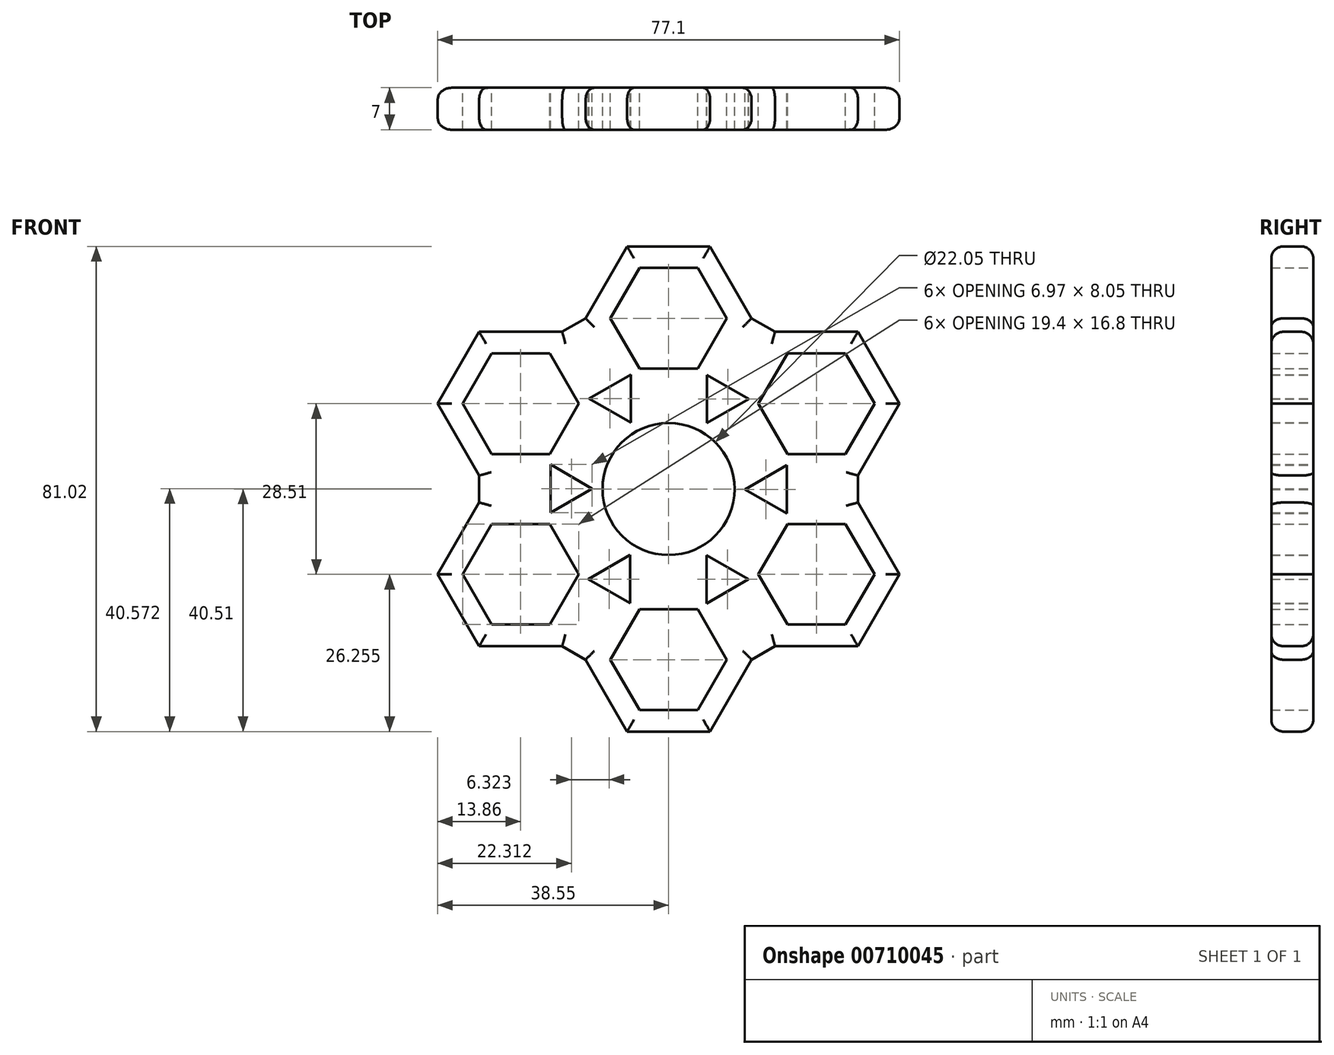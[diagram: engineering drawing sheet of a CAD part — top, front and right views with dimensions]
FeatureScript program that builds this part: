
annotation { "Feature Type Name" : "Feature", "Feature Type Description" : "" }
export const myFeature = defineFeature(function(context is Context, id is Id, definition is map)
    precondition{}
    {
        {
            var Q0;
            Q0=qCreatedBy(makeId("Front.planeOp"),FACE);
            var sketch = newSketch(context, id + "F0", { "sketchPlane" : qUnion([Q0])});
            skCircle(sketch, "E0", {"center": v(0, 0) * mm, "radius": 14.5 * mm});
            skCircle(sketch, "E1", {"center": v(0, 0) * mm, "radius": 11.03 * mm});
            skCircle(sketch, "E2.cCircle", {"center": v(0, 28.5) * mm, "radius": 8.4 * mm, "construction": true});
            skLineSegment(sketch, "E2.0", {"start": v(4.85, 20.1) * mm, "end": v(-4.85, 20.1) * mm});
            skLineSegment(sketch, "E2.1", {"start": v(-4.85, 20.1) * mm, "end": v(-9.7, 28.5) * mm});
            skLineSegment(sketch, "E2.2", {"start": v(-9.7, 28.5) * mm, "end": v(-4.85, 36.9) * mm});
            skLineSegment(sketch, "E2.3", {"start": v(-4.85, 36.9) * mm, "end": v(4.85, 36.9) * mm});
            skLineSegment(sketch, "E2.4", {"start": v(4.85, 36.9) * mm, "end": v(9.7, 28.5) * mm});
            skLineSegment(sketch, "E2.5", {"start": v(9.7, 28.5) * mm, "end": v(4.85, 20.1) * mm});
            skPoint(sketch, "E2.0.midPoint", {"position": v(0, 20.1) * mm});
            skCircle(sketch, "E3.cCircle", {"center": v(0, 28.5) * mm, "radius": 12 * mm, "construction": true});
            skLineSegment(sketch, "E3.0", {"start": v(6.93, 16.5) * mm, "end": v(-6.93, 16.5) * mm});
            skLineSegment(sketch, "E3.1", {"start": v(-6.93, 16.5) * mm, "end": v(-13.86, 28.5) * mm});
            skLineSegment(sketch, "E3.2", {"start": v(-13.86, 28.5) * mm, "end": v(-6.93, 40.5) * mm});
            skLineSegment(sketch, "E3.3", {"start": v(-6.93, 40.5) * mm, "end": v(6.93, 40.5) * mm});
            skLineSegment(sketch, "E3.4", {"start": v(6.93, 40.5) * mm, "end": v(13.86, 28.5) * mm});
            skLineSegment(sketch, "E3.5", {"start": v(13.86, 28.5) * mm, "end": v(6.93, 16.5) * mm});
            skPoint(sketch, "E3.0.midPoint", {"position": v(0, 16.5) * mm});
            skLineSegment(sketch, "E4.1.0", {"start": v(-17.76, 26.25) * mm, "end": v(-10.83, 14.25) * mm});
            skPoint(sketch, "E4.1.2", {"position": v(-17.42, 10.05) * mm});
            skLineSegment(sketch, "E4.1.3", {"start": v(-31.62, 2.25) * mm, "end": v(-38.55, 14.25) * mm});
            skLineSegment(sketch, "E4.1.4", {"start": v(-17.76, 2.25) * mm, "end": v(-31.62, 2.25) * mm});
            skCircle(sketch, "E4.1.5", {"center": v(-24.7, 14.25) * mm, "radius": 12 * mm, "construction": true});
            skPoint(sketch, "E4.1.7", {"position": v(-14.3, 8.25) * mm});
            skCircle(sketch, "E4.1.8", {"center": v(-24.7, 14.25) * mm, "radius": 8.4 * mm, "construction": true});
            skLineSegment(sketch, "E4.1.9", {"start": v(-29.54, 22.65) * mm, "end": v(-19.84, 22.65) * mm});
            skLineSegment(sketch, "E4.1.10", {"start": v(-29.54, 5.85) * mm, "end": v(-34.39, 14.25) * mm});
            skLineSegment(sketch, "E4.1.11", {"start": v(-38.55, 14.25) * mm, "end": v(-31.62, 26.25) * mm});
            skLineSegment(sketch, "E4.1.12", {"start": v(-10.83, 14.25) * mm, "end": v(-17.76, 2.25) * mm});
            skLineSegment(sketch, "E4.1.13", {"start": v(-15, 14.25) * mm, "end": v(-19.84, 5.85) * mm});
            skLineSegment(sketch, "E4.1.14", {"start": v(-19.84, 22.65) * mm, "end": v(-15, 14.25) * mm});
            skLineSegment(sketch, "E4.1.15", {"start": v(-31.62, 26.25) * mm, "end": v(-17.76, 26.25) * mm});
            skLineSegment(sketch, "E4.1.16", {"start": v(-34.39, 14.25) * mm, "end": v(-29.54, 22.65) * mm});
            skLineSegment(sketch, "E4.1.17", {"start": v(-19.84, 5.85) * mm, "end": v(-29.54, 5.85) * mm});
            skLineSegment(sketch, "E4.2.0", {"start": v(-31.62, -2.25) * mm, "end": v(-17.76, -2.25) * mm});
            skPoint(sketch, "E4.2.2", {"position": v(-17.42, -10.05) * mm});
            skLineSegment(sketch, "E4.2.3", {"start": v(-17.76, -26.25) * mm, "end": v(-31.62, -26.25) * mm});
            skLineSegment(sketch, "E4.2.4", {"start": v(-10.83, -14.25) * mm, "end": v(-17.76, -26.25) * mm});
            skCircle(sketch, "E4.2.5", {"center": v(-24.7, -14.25) * mm, "radius": 12 * mm, "construction": true});
            skPoint(sketch, "E4.2.7", {"position": v(-14.3, -8.25) * mm});
            skCircle(sketch, "E4.2.8", {"center": v(-24.7, -14.25) * mm, "radius": 8.4 * mm, "construction": true});
            skLineSegment(sketch, "E4.2.9", {"start": v(-34.39, -14.25) * mm, "end": v(-29.54, -5.85) * mm});
            skLineSegment(sketch, "E4.2.10", {"start": v(-19.84, -22.65) * mm, "end": v(-29.54, -22.65) * mm});
            skLineSegment(sketch, "E4.2.11", {"start": v(-31.62, -26.25) * mm, "end": v(-38.55, -14.25) * mm});
            skLineSegment(sketch, "E4.2.12", {"start": v(-17.76, -2.25) * mm, "end": v(-10.83, -14.25) * mm});
            skLineSegment(sketch, "E4.2.13", {"start": v(-19.84, -5.85) * mm, "end": v(-15, -14.25) * mm});
            skLineSegment(sketch, "E4.2.14", {"start": v(-29.54, -5.85) * mm, "end": v(-19.84, -5.85) * mm});
            skLineSegment(sketch, "E4.2.15", {"start": v(-38.55, -14.25) * mm, "end": v(-31.62, -2.25) * mm});
            skLineSegment(sketch, "E4.2.16", {"start": v(-29.54, -22.65) * mm, "end": v(-34.39, -14.25) * mm});
            skLineSegment(sketch, "E4.2.17", {"start": v(-15, -14.25) * mm, "end": v(-19.84, -22.65) * mm});
            skLineSegment(sketch, "E4.3.0", {"start": v(-13.86, -28.5) * mm, "end": v(-6.93, -16.5) * mm});
            skPoint(sketch, "E4.3.2", {"position": v(0, -20.1) * mm});
            skLineSegment(sketch, "E4.3.3", {"start": v(13.86, -28.5) * mm, "end": v(6.93, -40.5) * mm});
            skLineSegment(sketch, "E4.3.4", {"start": v(6.93, -16.5) * mm, "end": v(13.86, -28.5) * mm});
            skCircle(sketch, "E4.3.5", {"center": v(0, -28.5) * mm, "radius": 12 * mm, "construction": true});
            skPoint(sketch, "E4.3.7", {"position": v(0, -16.5) * mm});
            skCircle(sketch, "E4.3.8", {"center": v(0, -28.5) * mm, "radius": 8.4 * mm, "construction": true});
            skLineSegment(sketch, "E4.3.9", {"start": v(-4.85, -36.9) * mm, "end": v(-9.7, -28.5) * mm});
            skLineSegment(sketch, "E4.3.10", {"start": v(9.7, -28.5) * mm, "end": v(4.85, -36.9) * mm});
            skLineSegment(sketch, "E4.3.11", {"start": v(6.93, -40.5) * mm, "end": v(-6.93, -40.5) * mm});
            skLineSegment(sketch, "E4.3.12", {"start": v(-6.93, -16.5) * mm, "end": v(6.93, -16.5) * mm});
            skLineSegment(sketch, "E4.3.13", {"start": v(-4.85, -20.1) * mm, "end": v(4.85, -20.1) * mm});
            skLineSegment(sketch, "E4.3.14", {"start": v(-9.7, -28.5) * mm, "end": v(-4.85, -20.1) * mm});
            skLineSegment(sketch, "E4.3.15", {"start": v(-6.93, -40.5) * mm, "end": v(-13.86, -28.5) * mm});
            skLineSegment(sketch, "E4.3.16", {"start": v(4.85, -36.9) * mm, "end": v(-4.85, -36.9) * mm});
            skLineSegment(sketch, "E4.3.17", {"start": v(4.85, -20.1) * mm, "end": v(9.7, -28.5) * mm});
            skLineSegment(sketch, "E4.4.0", {"start": v(17.76, -26.25) * mm, "end": v(10.83, -14.25) * mm});
            skPoint(sketch, "E4.4.2", {"position": v(17.42, -10.05) * mm});
            skLineSegment(sketch, "E4.4.3", {"start": v(31.62, -2.25) * mm, "end": v(38.55, -14.25) * mm});
            skLineSegment(sketch, "E4.4.4", {"start": v(17.76, -2.25) * mm, "end": v(31.62, -2.25) * mm});
            skCircle(sketch, "E4.4.5", {"center": v(24.7, -14.25) * mm, "radius": 12 * mm, "construction": true});
            skPoint(sketch, "E4.4.7", {"position": v(14.3, -8.25) * mm});
            skCircle(sketch, "E4.4.8", {"center": v(24.7, -14.25) * mm, "radius": 8.4 * mm, "construction": true});
            skLineSegment(sketch, "E4.4.9", {"start": v(29.54, -22.65) * mm, "end": v(19.84, -22.65) * mm});
            skLineSegment(sketch, "E4.4.10", {"start": v(29.54, -5.85) * mm, "end": v(34.39, -14.25) * mm});
            skLineSegment(sketch, "E4.4.11", {"start": v(38.55, -14.25) * mm, "end": v(31.62, -26.25) * mm});
            skLineSegment(sketch, "E4.4.12", {"start": v(10.83, -14.25) * mm, "end": v(17.76, -2.25) * mm});
            skLineSegment(sketch, "E4.4.13", {"start": v(15, -14.25) * mm, "end": v(19.84, -5.85) * mm});
            skLineSegment(sketch, "E4.4.14", {"start": v(19.84, -22.65) * mm, "end": v(15, -14.25) * mm});
            skLineSegment(sketch, "E4.4.15", {"start": v(31.62, -26.25) * mm, "end": v(17.76, -26.25) * mm});
            skLineSegment(sketch, "E4.4.16", {"start": v(34.39, -14.25) * mm, "end": v(29.54, -22.65) * mm});
            skLineSegment(sketch, "E4.4.17", {"start": v(19.84, -5.85) * mm, "end": v(29.54, -5.85) * mm});
            skLineSegment(sketch, "E4.5.0", {"start": v(31.62, 2.25) * mm, "end": v(17.76, 2.25) * mm});
            skPoint(sketch, "E4.5.2", {"position": v(17.42, 10.05) * mm});
            skLineSegment(sketch, "E4.5.3", {"start": v(17.76, 26.25) * mm, "end": v(31.62, 26.25) * mm});
            skLineSegment(sketch, "E4.5.4", {"start": v(10.83, 14.25) * mm, "end": v(17.76, 26.25) * mm});
            skCircle(sketch, "E4.5.5", {"center": v(24.7, 14.25) * mm, "radius": 12 * mm, "construction": true});
            skPoint(sketch, "E4.5.7", {"position": v(14.3, 8.25) * mm});
            skCircle(sketch, "E4.5.8", {"center": v(24.7, 14.25) * mm, "radius": 8.4 * mm, "construction": true});
            skLineSegment(sketch, "E4.5.9", {"start": v(34.39, 14.25) * mm, "end": v(29.54, 5.85) * mm});
            skLineSegment(sketch, "E4.5.10", {"start": v(19.84, 22.65) * mm, "end": v(29.54, 22.65) * mm});
            skLineSegment(sketch, "E4.5.11", {"start": v(31.62, 26.25) * mm, "end": v(38.55, 14.25) * mm});
            skLineSegment(sketch, "E4.5.12", {"start": v(17.76, 2.25) * mm, "end": v(10.83, 14.25) * mm});
            skLineSegment(sketch, "E4.5.13", {"start": v(19.84, 5.85) * mm, "end": v(15, 14.25) * mm});
            skLineSegment(sketch, "E4.5.14", {"start": v(29.54, 5.85) * mm, "end": v(19.84, 5.85) * mm});
            skLineSegment(sketch, "E4.5.15", {"start": v(38.55, 14.25) * mm, "end": v(31.62, 2.25) * mm});
            skLineSegment(sketch, "E4.5.16", {"start": v(29.54, 22.65) * mm, "end": v(34.39, 14.25) * mm});
            skLineSegment(sketch, "E4.5.17", {"start": v(15, 14.25) * mm, "end": v(19.84, 22.65) * mm});
            skLineSegment(sketch, "E5", {"start": v(13.86, 28.5) * mm, "end": v(17.76, 26.25) * mm});
            skLineSegment(sketch, "E6.1.0", {"start": v(-17.76, 26.25) * mm, "end": v(-13.86, 28.5) * mm});
            skLineSegment(sketch, "E6.2.0", {"start": v(-31.62, -2.25) * mm, "end": v(-31.62, 2.25) * mm});
            skLineSegment(sketch, "E6.3.0", {"start": v(-13.86, -28.5) * mm, "end": v(-17.76, -26.25) * mm});
            skLineSegment(sketch, "E6.4.0", {"start": v(17.76, -26.25) * mm, "end": v(13.86, -28.5) * mm});
            skLineSegment(sketch, "E6.5.0", {"start": v(31.62, 2.25) * mm, "end": v(31.62, -2.25) * mm});
            skSolve(sketch);
        }
        {
            var Q0;
            Q0 = qSketchRegion(id + "F0", true);
            var Q1;
            Q1=makeQuery(id+"F0.imprint","IMPRINT",FACE,{"disambiguationData":[TD([[makeQuery(id+"F0.imprint","IMPRINT",EDGE,{"derivedFrom":sQuery(id+"F0.wireOp",EDGE,"E0")}),1.0]])]});
            extrude(context, id + "F1", {"entities" : qUnion([Q0, Q1]), "depth" : 7 * mm, "offsetDistance" : 25 * mm});
        }
        {
            var Q0;
            Q0=makeQuery(id+"F1.opExtrude","CAP_EDGE",EDGE,{"disambiguationData":[OSD([sQuery(id+"F0.wireOp",EDGE,"E3.3")])],"isStart":false});
            var Q1;
            Q1=makeQuery(id+"F1.opExtrude","CAP_EDGE",EDGE,{"disambiguationData":[OSD([sQuery(id+"F0.wireOp",EDGE,"E3.4")])],"isStart":false});
            var Q2;
            Q2=makeQuery(id+"F1.opExtrude","CAP_EDGE",EDGE,{"disambiguationData":[OSD([sQuery(id+"F0.wireOp",EDGE,"6zvGGHwx-PwQj-7mVk-bG3N-4MqW4xq4l6px")])],"isStart":false});
            var Q3;
            Q3=makeQuery(id+"F1.opExtrude","CAP_EDGE",EDGE,{"disambiguationData":[OSD([sQuery(id+"F0.wireOp",EDGE,"E4.5.3")])],"isStart":false});
            var Q4;
            Q4=makeQuery(id+"F1.opExtrude","CAP_EDGE",EDGE,{"disambiguationData":[OSD([sQuery(id+"F0.wireOp",EDGE,"E4.5.11")])],"isStart":false});
            var Q5;
            Q5=makeQuery(id+"F1.opExtrude","CAP_EDGE",EDGE,{"disambiguationData":[OSD([sQuery(id+"F0.wireOp",EDGE,"E4.5.15")])],"isStart":false});
            var Q6;
            Q6=makeQuery(id+"F1.opExtrude","CAP_EDGE",EDGE,{"disambiguationData":[OSD([sQuery(id+"F0.wireOp",EDGE,"2094d824-f66e-4dc5-9a7e-ccef21a2b5a5.5.0")])],"isStart":false});
            var Q7;
            Q7=makeQuery(id+"F1.opExtrude","CAP_EDGE",EDGE,{"disambiguationData":[OSD([sQuery(id+"F0.wireOp",EDGE,"E4.4.3")])],"isStart":false});
            var Q8;
            Q8=makeQuery(id+"F1.opExtrude","CAP_EDGE",EDGE,{"disambiguationData":[OSD([sQuery(id+"F0.wireOp",EDGE,"E4.4.11")])],"isStart":false});
            var Q9;
            Q9=makeQuery(id+"F1.opExtrude","CAP_EDGE",EDGE,{"disambiguationData":[OSD([sQuery(id+"F0.wireOp",EDGE,"E4.4.15")])],"isStart":false});
            var Q10;
            Q10=makeQuery(id+"F1.opExtrude","CAP_EDGE",EDGE,{"disambiguationData":[OSD([sQuery(id+"F0.wireOp",EDGE,"2094d824-f66e-4dc5-9a7e-ccef21a2b5a5.4.0")])],"isStart":false});
            var Q11;
            Q11=makeQuery(id+"F1.opExtrude","CAP_EDGE",EDGE,{"disambiguationData":[OSD([sQuery(id+"F0.wireOp",EDGE,"E4.3.3")])],"isStart":false});
            var Q12;
            Q12=makeQuery(id+"F1.opExtrude","CAP_EDGE",EDGE,{"disambiguationData":[OSD([sQuery(id+"F0.wireOp",EDGE,"E4.3.11")])],"isStart":false});
            var Q13;
            Q13=makeQuery(id+"F1.opExtrude","CAP_EDGE",EDGE,{"disambiguationData":[OSD([sQuery(id+"F0.wireOp",EDGE,"E4.3.15")])],"isStart":false});
            var Q14;
            Q14=makeQuery(id+"F1.opExtrude","CAP_EDGE",EDGE,{"disambiguationData":[OSD([sQuery(id+"F0.wireOp",EDGE,"2094d824-f66e-4dc5-9a7e-ccef21a2b5a5.3.0")])],"isStart":false});
            var Q15;
            Q15=makeQuery(id+"F1.opExtrude","CAP_EDGE",EDGE,{"disambiguationData":[OSD([sQuery(id+"F0.wireOp",EDGE,"E4.2.3")])],"isStart":false});
            var Q16;
            Q16=makeQuery(id+"F1.opExtrude","CAP_EDGE",EDGE,{"disambiguationData":[OSD([sQuery(id+"F0.wireOp",EDGE,"E4.2.11")])],"isStart":false});
            var Q17;
            Q17=makeQuery(id+"F1.opExtrude","CAP_EDGE",EDGE,{"disambiguationData":[OSD([sQuery(id+"F0.wireOp",EDGE,"E4.2.15")])],"isStart":false});
            var Q18;
            Q18=makeQuery(id+"F1.opExtrude","CAP_EDGE",EDGE,{"disambiguationData":[OSD([sQuery(id+"F0.wireOp",EDGE,"2094d824-f66e-4dc5-9a7e-ccef21a2b5a5.2.0")])],"isStart":false});
            var Q19;
            Q19=makeQuery(id+"F1.opExtrude","CAP_EDGE",EDGE,{"disambiguationData":[OSD([sQuery(id+"F0.wireOp",EDGE,"E4.1.3")])],"isStart":false});
            var Q20;
            Q20=makeQuery(id+"F1.opExtrude","CAP_EDGE",EDGE,{"disambiguationData":[OSD([sQuery(id+"F0.wireOp",EDGE,"E4.1.11")])],"isStart":false});
            var Q21;
            Q21=makeQuery(id+"F1.opExtrude","CAP_EDGE",EDGE,{"disambiguationData":[OSD([sQuery(id+"F0.wireOp",EDGE,"E4.1.15")])],"isStart":false});
            var Q22;
            Q22=makeQuery(id+"F1.opExtrude","CAP_EDGE",EDGE,{"disambiguationData":[OSD([sQuery(id+"F0.wireOp",EDGE,"2094d824-f66e-4dc5-9a7e-ccef21a2b5a5.1.0")])],"isStart":false});
            var Q23;
            Q23=makeQuery(id+"F1.opExtrude","CAP_EDGE",EDGE,{"disambiguationData":[OSD([sQuery(id+"F0.wireOp",EDGE,"E3.2")])],"isStart":false});
            var Q24;
            Q24=makeQuery(id+"F1.opExtrude","CAP_EDGE",EDGE,{"disambiguationData":[OSD([sQuery(id+"F0.wireOp",EDGE,"2094d824-f66e-4dc5-9a7e-ccef21a2b5a5.3.0")])],"isStart":true});
            var Q25;
            Q25=makeQuery(id+"F1.opExtrude","CAP_EDGE",EDGE,{"disambiguationData":[OSD([sQuery(id+"F0.wireOp",EDGE,"E4.3.15")])],"isStart":true});
            var Q26;
            Q26=makeQuery(id+"F1.opExtrude","CAP_EDGE",EDGE,{"disambiguationData":[OSD([sQuery(id+"F0.wireOp",EDGE,"E4.3.3")])],"isStart":true});
            var Q27;
            Q27=makeQuery(id+"F1.opExtrude","CAP_EDGE",EDGE,{"disambiguationData":[OSD([sQuery(id+"F0.wireOp",EDGE,"2094d824-f66e-4dc5-9a7e-ccef21a2b5a5.4.0")])],"isStart":true});
            var Q28;
            Q28=makeQuery(id+"F1.opExtrude","CAP_EDGE",EDGE,{"disambiguationData":[OSD([sQuery(id+"F0.wireOp",EDGE,"E4.4.15")])],"isStart":true});
            var Q29;
            Q29=makeQuery(id+"F1.opExtrude","CAP_EDGE",EDGE,{"disambiguationData":[OSD([sQuery(id+"F0.wireOp",EDGE,"E4.4.11")])],"isStart":true});
            var Q30;
            Q30=makeQuery(id+"F1.opExtrude","CAP_EDGE",EDGE,{"disambiguationData":[OSD([sQuery(id+"F0.wireOp",EDGE,"E4.4.3")])],"isStart":true});
            var Q31;
            Q31=makeQuery(id+"F1.opExtrude","CAP_EDGE",EDGE,{"disambiguationData":[OSD([sQuery(id+"F0.wireOp",EDGE,"2094d824-f66e-4dc5-9a7e-ccef21a2b5a5.5.0")])],"isStart":true});
            var Q32;
            Q32=makeQuery(id+"F1.opExtrude","CAP_EDGE",EDGE,{"disambiguationData":[OSD([sQuery(id+"F0.wireOp",EDGE,"E4.5.15")])],"isStart":true});
            var Q33;
            Q33=makeQuery(id+"F1.opExtrude","CAP_EDGE",EDGE,{"disambiguationData":[OSD([sQuery(id+"F0.wireOp",EDGE,"E4.5.11")])],"isStart":true});
            var Q34;
            Q34=makeQuery(id+"F1.opExtrude","CAP_EDGE",EDGE,{"disambiguationData":[OSD([sQuery(id+"F0.wireOp",EDGE,"E4.5.3")])],"isStart":true});
            var Q35;
            Q35=makeQuery(id+"F1.opExtrude","CAP_EDGE",EDGE,{"disambiguationData":[OSD([sQuery(id+"F0.wireOp",EDGE,"6zvGGHwx-PwQj-7mVk-bG3N-4MqW4xq4l6px")])],"isStart":true});
            var Q36;
            Q36=makeQuery(id+"F1.opExtrude","CAP_EDGE",EDGE,{"disambiguationData":[OSD([sQuery(id+"F0.wireOp",EDGE,"E3.4")])],"isStart":true});
            var Q37;
            Q37=makeQuery(id+"F1.opExtrude","CAP_EDGE",EDGE,{"disambiguationData":[OSD([sQuery(id+"F0.wireOp",EDGE,"2094d824-f66e-4dc5-9a7e-ccef21a2b5a5.1.0")])],"isStart":true});
            var Q38;
            Q38=makeQuery(id+"F1.opExtrude","CAP_EDGE",EDGE,{"disambiguationData":[OSD([sQuery(id+"F0.wireOp",EDGE,"E4.1.15")])],"isStart":true});
            var Q39;
            Q39=makeQuery(id+"F1.opExtrude","CAP_EDGE",EDGE,{"disambiguationData":[OSD([sQuery(id+"F0.wireOp",EDGE,"E4.1.11")])],"isStart":true});
            var Q40;
            Q40=makeQuery(id+"F1.opExtrude","CAP_EDGE",EDGE,{"disambiguationData":[OSD([sQuery(id+"F0.wireOp",EDGE,"E4.1.3")])],"isStart":true});
            var Q41;
            Q41=makeQuery(id+"F1.opExtrude","CAP_EDGE",EDGE,{"disambiguationData":[OSD([sQuery(id+"F0.wireOp",EDGE,"2094d824-f66e-4dc5-9a7e-ccef21a2b5a5.2.0")])],"isStart":true});
            var Q42;
            Q42=makeQuery(id+"F1.opExtrude","CAP_EDGE",EDGE,{"disambiguationData":[OSD([sQuery(id+"F0.wireOp",EDGE,"E4.2.15")])],"isStart":true});
            var Q43;
            Q43=makeQuery(id+"F1.opExtrude","CAP_EDGE",EDGE,{"disambiguationData":[OSD([sQuery(id+"F0.wireOp",EDGE,"E4.2.11")])],"isStart":true});
            var Q44;
            Q44=makeQuery(id+"F1.opExtrude","CAP_EDGE",EDGE,{"disambiguationData":[OSD([sQuery(id+"F0.wireOp",EDGE,"E4.2.3")])],"isStart":true});
            var Q45;
            Q45=makeQuery(id+"F1.opExtrude","CAP_EDGE",EDGE,{"disambiguationData":[OSD([sQuery(id+"F0.wireOp",EDGE,"E4.3.11")])],"isStart":true});
            var Q46;
            Q46=makeQuery(id+"F1.opExtrude","CAP_EDGE",EDGE,{"disambiguationData":[OSD([sQuery(id+"F0.wireOp",EDGE,"E3.2")])],"isStart":true});
            var Q47;
            Q47=makeQuery(id+"F1.opExtrude","CAP_EDGE",EDGE,{"disambiguationData":[OSD([sQuery(id+"F0.wireOp",EDGE,"E3.3")])],"isStart":true});
            var Q48;
            Q48=makeQuery(id+"F1.opExtrude","CAP_EDGE",EDGE,{"disambiguationData":[OSD([sQuery(id+"F0.wireOp",EDGE,"E6.1.0")])],"isStart":false});
            var Q49;
            Q49=makeQuery(id+"F1.opExtrude","CAP_EDGE",EDGE,{"disambiguationData":[OSD([sQuery(id+"F0.wireOp",EDGE,"E5")])],"isStart":false});
            var Q50;
            Q50=makeQuery(id+"F1.opExtrude","CAP_EDGE",EDGE,{"disambiguationData":[OSD([sQuery(id+"F0.wireOp",EDGE,"E6.5.0")])],"isStart":false});
            var Q51;
            Q51=makeQuery(id+"F1.opExtrude","CAP_EDGE",EDGE,{"disambiguationData":[OSD([sQuery(id+"F0.wireOp",EDGE,"E6.4.0")])],"isStart":false});
            var Q52;
            Q52=makeQuery(id+"F1.opExtrude","CAP_EDGE",EDGE,{"disambiguationData":[OSD([sQuery(id+"F0.wireOp",EDGE,"E6.3.0")])],"isStart":false});
            var Q53;
            Q53=makeQuery(id+"F1.opExtrude","CAP_EDGE",EDGE,{"disambiguationData":[OSD([sQuery(id+"F0.wireOp",EDGE,"E6.2.0")])],"isStart":false});
            var Q54;
            Q54=makeQuery(id+"F1.opExtrude","CAP_EDGE",EDGE,{"disambiguationData":[OSD([sQuery(id+"F0.wireOp",EDGE,"E6.1.0")])],"isStart":true});
            var Q55;
            Q55=makeQuery(id+"F1.opExtrude","CAP_EDGE",EDGE,{"disambiguationData":[OSD([sQuery(id+"F0.wireOp",EDGE,"E5")])],"isStart":true});
            var Q56;
            Q56=makeQuery(id+"F1.opExtrude","CAP_EDGE",EDGE,{"disambiguationData":[OSD([sQuery(id+"F0.wireOp",EDGE,"E6.5.0")])],"isStart":true});
            var Q57;
            Q57=makeQuery(id+"F1.opExtrude","CAP_EDGE",EDGE,{"disambiguationData":[OSD([sQuery(id+"F0.wireOp",EDGE,"E6.4.0")])],"isStart":true});
            var Q58;
            Q58=makeQuery(id+"F1.opExtrude","CAP_EDGE",EDGE,{"disambiguationData":[OSD([sQuery(id+"F0.wireOp",EDGE,"E6.3.0")])],"isStart":true});
            var Q59;
            Q59=makeQuery(id+"F1.opExtrude","CAP_EDGE",EDGE,{"disambiguationData":[OSD([sQuery(id+"F0.wireOp",EDGE,"E6.2.0")])],"isStart":true});
            fillet(context, id + "F2", {"entities" : qUnion([Q0, Q1, Q2, Q3, Q4, Q5, Q6, Q7, Q8, Q9, Q10, Q11, Q12, Q13, Q14, Q15, Q16, Q17, Q18, Q19, Q20, Q21, Q22, Q23, Q24, Q25, Q26, Q27, Q28, Q29, Q30, Q31, Q32, Q33, Q34, Q35, Q36, Q37, Q38, Q39, Q40, Q41, Q42, Q43, Q44, Q45, Q46, Q47, Q48, Q49, Q50, Q51, Q52, Q53, Q54, Q55, Q56, Q57, Q58, Q59]), "radius" : 2 * mm, "tangentPropagation" : true, "allowEdgeOverflow" : false});
        }
        {
            var Q0;
            Q0=qCreatedBy(makeId("Front.planeOp"),FACE);
            var sketch = newSketch(context, id + "F3", { "sketchPlane" : qUnion([Q0])});
            skCircle(sketch, "E7.cCircle", {"center": v(-8.65, 15.1) * mm, "radius": 2.32 * mm, "construction": true});
            skLineSegment(sketch, "E7.0", {"start": v(-6.32, 19.12) * mm, "end": v(-6.32, 11.08) * mm});
            skLineSegment(sketch, "E7.1", {"start": v(-6.32, 11.08) * mm, "end": v(-13.3, 15.1) * mm});
            skLineSegment(sketch, "E7.2", {"start": v(-13.3, 15.1) * mm, "end": v(-6.32, 19.12) * mm});
            skPoint(sketch, "E7.0.midPoint", {"position": v(-6.32, 15.1) * mm});
            skCircle(sketch, "E8.1.0", {"center": v(-17.4, 0.06) * mm, "radius": 2.32 * mm, "construction": true});
            skLineSegment(sketch, "E8.1.1", {"start": v(-19.72, -3.96) * mm, "end": v(-19.72, 4.08) * mm});
            skLineSegment(sketch, "E8.1.2", {"start": v(-12.75, 0.06) * mm, "end": v(-19.72, -3.96) * mm});
            skLineSegment(sketch, "E8.1.3", {"start": v(-19.72, 4.08) * mm, "end": v(-12.75, 0.06) * mm});
            skCircle(sketch, "E8.2.0", {"center": v(-8.75, -15.04) * mm, "radius": 2.32 * mm, "construction": true});
            skLineSegment(sketch, "E8.2.1", {"start": v(-6.43, -19.06) * mm, "end": v(-13.4, -15.04) * mm});
            skLineSegment(sketch, "E8.2.2", {"start": v(-6.43, -11.01) * mm, "end": v(-6.43, -19.06) * mm});
            skLineSegment(sketch, "E8.2.3", {"start": v(-13.4, -15.04) * mm, "end": v(-6.43, -11.01) * mm});
            skCircle(sketch, "E8.3.0", {"center": v(8.65, -15.1) * mm, "radius": 2.32 * mm, "construction": true});
            skLineSegment(sketch, "E8.3.1", {"start": v(13.3, -15.1) * mm, "end": v(6.32, -19.12) * mm});
            skLineSegment(sketch, "E8.3.2", {"start": v(6.32, -11.08) * mm, "end": v(13.3, -15.1) * mm});
            skLineSegment(sketch, "E8.3.3", {"start": v(6.32, -19.12) * mm, "end": v(6.32, -11.08) * mm});
            skCircle(sketch, "E8.4.0", {"center": v(17.4, -0.06) * mm, "radius": 2.32 * mm, "construction": true});
            skLineSegment(sketch, "E8.4.1", {"start": v(19.72, 3.96) * mm, "end": v(19.72, -4.08) * mm});
            skLineSegment(sketch, "E8.4.2", {"start": v(12.75, -0.06) * mm, "end": v(19.72, 3.96) * mm});
            skLineSegment(sketch, "E8.4.3", {"start": v(19.72, -4.08) * mm, "end": v(12.75, -0.06) * mm});
            skPoint(sketch, "E8.center", {"position": v(0, 0) * mm});
            skCircle(sketch, "E9.1.5.0", {"center": v(8.75, 15.04) * mm, "radius": 2.32 * mm, "construction": true});
            skLineSegment(sketch, "E9.2.5.0", {"start": v(6.43, 19.06) * mm, "end": v(13.4, 15.04) * mm});
            skLineSegment(sketch, "E9.5.5.0", {"start": v(6.43, 11.01) * mm, "end": v(6.43, 19.06) * mm});
            skLineSegment(sketch, "E9.8.5.0", {"start": v(13.4, 15.04) * mm, "end": v(6.43, 11.01) * mm});
            skSolve(sketch);
        }
        {
            var Q0;
            Q0 = qSketchRegion(id + "F3", true);
            extrude(context, id + "F4", {"entities" : qUnion([Q0]), "operationType" : NewBodyOperationType.REMOVE, "oppositeDirection" : true, "depth" : -7 * mm, "offsetDistance" : 25 * mm});
        }
    });
